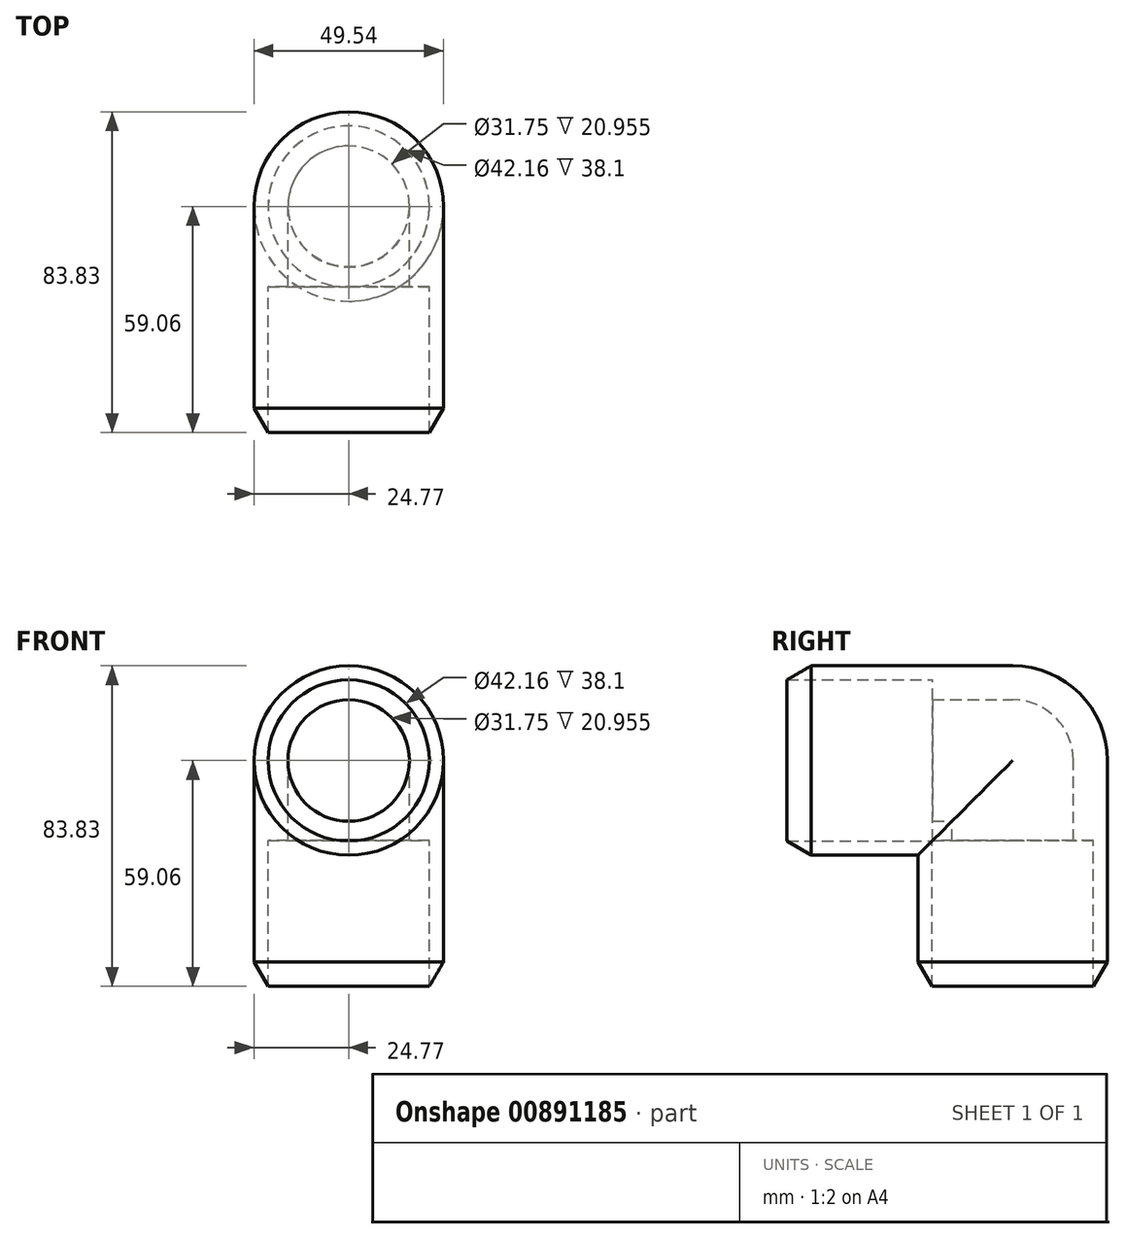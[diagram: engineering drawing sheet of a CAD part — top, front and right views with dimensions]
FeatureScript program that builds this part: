
annotation { "Feature Type Name" : "Feature", "Feature Type Description" : "" }
export const myFeature = defineFeature(function(context is Context, id is Id, definition is map)
    precondition{}
    {
        {
            var Q0;
            Q0=qCreatedBy(makeId("Right.planeOp"),FACE);
            var sketch = newSketch(context, id + "F0", { "sketchPlane" : qUnion([Q0])});
            skLineSegment(sketch, "E0", {"start": v(-59.06, 21.08) * mm, "end": v(-20.96, 21.08) * mm});
            skLineSegment(sketch, "E1", {"start": v(-20.96, 21.08) * mm, "end": v(-20.96, 15.88) * mm});
            skLineSegment(sketch, "E2", {"start": v(-20.96, 15.88) * mm, "end": v(0, 15.88) * mm});
            skLineSegment(sketch, "E3", {"start": v(15.87, 0) * mm, "end": v(15.87, 0) * mm});
            skLineSegment(sketch, "E4", {"start": v(15.87, 0) * mm, "end": v(24.77, 0) * mm});
            skLineSegment(sketch, "E5", {"start": v(24.77, 0) * mm, "end": v(24.77, 0) * mm});
            skLineSegment(sketch, "E6", {"start": v(0, 24.77) * mm, "end": v(-52.68, 24.76) * mm});
            skLineSegment(sketch, "E7", {"start": v(-52.68, 24.76) * mm, "end": v(-59.06, 21.08) * mm});
            skArc(sketch, "E8.filletArc", {"start": v(24.77, 0) * mm, "mid": v(17.51, 17.51) * mm, "end": v(0, 24.77) * mm});
            skArc(sketch, "E9.filletArc", {"start": v(15.88, 0) * mm, "mid": v(11.23, 11.23) * mm, "end": v(0, 15.88) * mm});
            skLineSegment(sketch, "E10", {"start": v(0, 0) * mm, "end": v(0, -11.7) * mm});
            skLineSegment(sketch, "E11", {"start": v(0, 0) * mm, "end": v(10.52, 0) * mm});
            skLineSegment(sketch, "E12", {"start": v(-59.06, 21.08) * mm, "end": v(-59.06, 0) * mm});
            skLineSegment(sketch, "E13", {"start": v(-59.06, 0) * mm, "end": v(15.87, 0) * mm});
            skSolve(sketch);
        }
        {
            var Q0;
            Q0=qCreatedBy(makeId("Right.planeOp"),FACE);
            var sketch = newSketch(context, id + "F1", { "sketchPlane" : qUnion([Q0])});
            skLineSegment(sketch, "E14", {"start": v(-21.08, -59.06) * mm, "end": v(-21.08, -20.96) * mm});
            skLineSegment(sketch, "E15", {"start": v(-21.08, -20.96) * mm, "end": v(-15.88, -20.96) * mm});
            skLineSegment(sketch, "E16", {"start": v(-15.88, -20.96) * mm, "end": v(-15.88, 0) * mm});
            skLineSegment(sketch, "E17", {"start": v(0, 15.88) * mm, "end": v(0, 15.88) * mm});
            skLineSegment(sketch, "E18", {"start": v(0, 15.88) * mm, "end": v(0, 24.77) * mm});
            skLineSegment(sketch, "E19", {"start": v(0, 24.77) * mm, "end": v(0, 24.77) * mm});
            skLineSegment(sketch, "E20", {"start": v(-24.77, 0) * mm, "end": v(-24.76, -52.68) * mm});
            skLineSegment(sketch, "E21", {"start": v(-24.76, -52.68) * mm, "end": v(-21.08, -59.06) * mm});
            skArc(sketch, "E22.filletArc", {"start": v(0, 24.77) * mm, "mid": v(-17.51, 17.51) * mm, "end": v(-24.77, 0) * mm});
            skArc(sketch, "E23.filletArc", {"start": v(0, 15.88) * mm, "mid": v(-11.23, 11.23) * mm, "end": v(-15.88, 0) * mm});
            skLineSegment(sketch, "E24", {"start": v(0, 36.04) * mm, "end": v(0, 0) * mm});
            skLineSegment(sketch, "E25", {"start": v(-2.18, 0) * mm, "end": v(0, 0) * mm});
            skLineSegment(sketch, "E26", {"start": v(-21.08, -59.06) * mm, "end": v(0, -59.06) * mm});
            skLineSegment(sketch, "E27", {"start": v(0, -59.06) * mm, "end": v(0, 15.88) * mm});
            skSolve(sketch);
        }
        {
            var Q0;
            Q0=qSketchRegion(id+"F0",true);
            var Q1;
            Q1=sQuery(id+"F0.wireOp",EDGE,"E13");
            revolve(context, id + "F2", {"surfaceOperationType" : NewSurfaceOperationType.NEW, "entities" : qUnion([Q0]), "axis" : qUnion([Q1]), "revolveType" : RevolveType.FULL});
        }
        {
            var Q0;
            {var subQ4=makeQuery(id+"F1.imprint","IMPRINT",EDGE,{"derivedFrom":sQuery(id+"F1.wireOp",EDGE,"E14")});Q0=qUnion([makeQuery(id+"F1.imprint","IMPRINT",FACE,{"disambiguationData":[TD([[subQ4,1.0]])]}),makeQuery(id+"F1.imprint","IMPRINT",FACE,{"disambiguationData":[TD([[subQ4,-1.0]])]})]);}
            var Q1;
            Q1=sQuery(id+"F1.wireOp",EDGE,"E27");
            revolve(context, id + "F3", {"operationType" : NewBodyOperationType.ADD, "surfaceOperationType" : NewSurfaceOperationType.NEW, "entities" : qUnion([Q0]), "axis" : qUnion([Q1]), "revolveType" : RevolveType.FULL});
        }
        {
            var Q0;
            Q0=makeQuery(id+"F0.imprint","IMPRINT",FACE,{"disambiguationData":[TD([[makeQuery(id+"F0.imprint","IMPRINT",EDGE,{"derivedFrom":sQuery(id+"F0.wireOp",EDGE,"E0")}),-1.0]])]});
            var Q1;
            Q1=sQuery(id+"F0.wireOp",EDGE,"E13");
            revolve(context, id + "F4", {"operationType" : NewBodyOperationType.REMOVE, "surfaceOperationType" : NewSurfaceOperationType.NEW, "entities" : qUnion([Q0]), "axis" : qUnion([Q1]), "revolveType" : RevolveType.FULL, "oppositeDirection" : true});
        }
        {
            var Q0;
            Q0=makeQuery(id+"F1.imprint","IMPRINT",FACE,{"disambiguationData":[TD([[makeQuery(id+"F1.imprint","IMPRINT",EDGE,{"derivedFrom":sQuery(id+"F1.wireOp",EDGE,"E14")}),-1.0]])]});
            var Q1;
            Q1=sQuery(id+"F1.wireOp",EDGE,"E27");
            revolve(context, id + "F5", {"operationType" : NewBodyOperationType.REMOVE, "surfaceOperationType" : NewSurfaceOperationType.NEW, "entities" : qUnion([Q0]), "axis" : qUnion([Q1]), "revolveType" : RevolveType.FULL, "oppositeDirection" : true});
        }
    });
